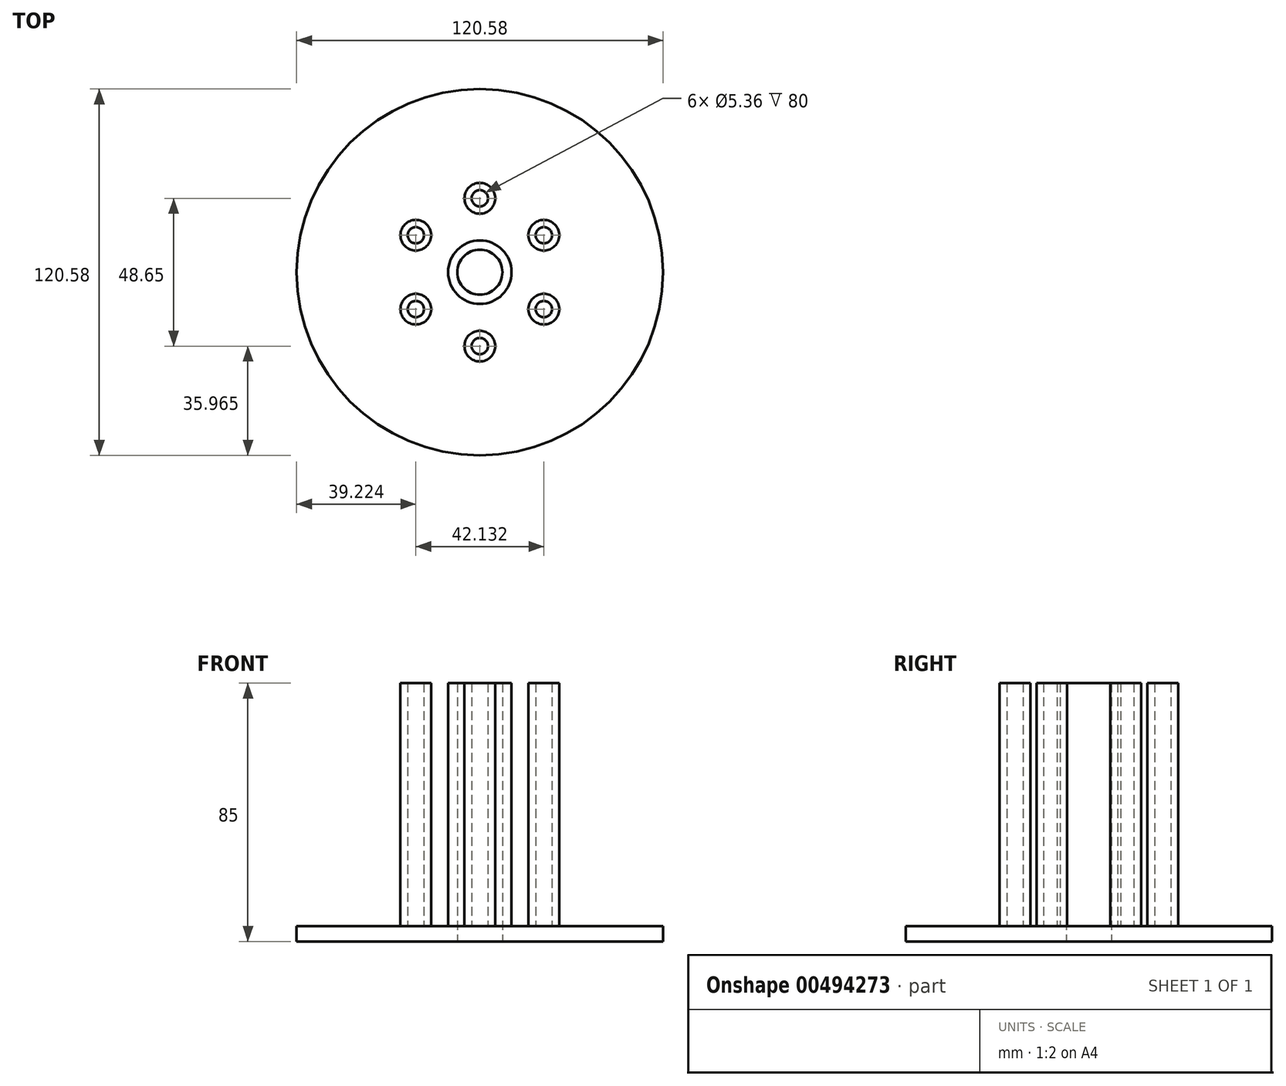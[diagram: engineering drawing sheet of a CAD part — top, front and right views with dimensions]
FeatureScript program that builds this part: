
annotation { "Feature Type Name" : "Feature", "Feature Type Description" : "" }
export const myFeature = defineFeature(function(context is Context, id is Id, definition is map)
    precondition{}
    {
        {
            var Q0;
            Q0=qCreatedBy(makeId("Top.planeOp"),FACE);
            var sketch = newSketch(context, id + "F0", { "sketchPlane" : qUnion([Q0])});
            skCircle(sketch, "E0", {"center": v(0, 0) * mm, "radius": 60.29 * mm});
            skCircle(sketch, "E1", {"center": v(0, 0) * mm, "radius": 7.42 * mm});
            skSolve(sketch);
        }
        {
            var Q0;
            Q0=makeQuery(id+"F0.imprint","IMPRINT",FACE,{"disambiguationData":[TD([[makeQuery(id+"F0.imprint","IMPRINT",EDGE,{"derivedFrom":sQuery(id+"F0.wireOp",EDGE,"E0")}),1.0]])]});
            extrude(context, id + "F1", {"entities" : qUnion([Q0]), "depth" : 5 * mm});
        }
        {
            var Q0;
            Q0=makeQuery(id+"F1.opExtrude","CAP_FACE",FACE,{"disambiguationData":[OSD([sQuery(id+"F0.wireOp",EDGE,"E0"),sQuery(id+"F0.wireOp",EDGE,"E1")])],"isStart":false});
            var sketch = newSketch(context, id + "F2", { "sketchPlane" : qUnion([Q0])});
            skCircle(sketch, "E2", {"center": v(0, 0) * mm, "radius": 10.45 * mm});
            skCircle(sketch, "E3", {"center": v(0, -24.32) * mm, "radius": 2.68 * mm});
            skCircle(sketch, "E4", {"center": v(0, -24.32) * mm, "radius": 5.06 * mm});
            skCircle(sketch, "E5.1.0", {"center": v(21.07, -12.16) * mm, "radius": 5.06 * mm});
            skCircle(sketch, "E5.1.1", {"center": v(21.07, -12.16) * mm, "radius": 2.68 * mm});
            skCircle(sketch, "E5.2.0", {"center": v(21.07, 12.16) * mm, "radius": 5.06 * mm});
            skCircle(sketch, "E5.2.1", {"center": v(21.07, 12.16) * mm, "radius": 2.68 * mm});
            skCircle(sketch, "E5.3.0", {"center": v(0, 24.32) * mm, "radius": 5.06 * mm});
            skCircle(sketch, "E5.3.1", {"center": v(0, 24.32) * mm, "radius": 2.68 * mm});
            skCircle(sketch, "E5.4.0", {"center": v(-21.07, 12.16) * mm, "radius": 5.06 * mm});
            skCircle(sketch, "E5.4.1", {"center": v(-21.07, 12.16) * mm, "radius": 2.68 * mm});
            skCircle(sketch, "E5.5.0", {"center": v(-21.07, -12.16) * mm, "radius": 5.06 * mm});
            skCircle(sketch, "E5.5.1", {"center": v(-21.07, -12.16) * mm, "radius": 2.68 * mm});
            skSolve(sketch);
        }
        {
            var Q0;
            Q0=makeQuery(id+"F2.imprint","IMPRINT",FACE,{"disambiguationData":[TD([[makeQuery(id+"F2.imprint","IMPRINT",EDGE,{"derivedFrom":sQuery(id+"F2.wireOp",EDGE,"E2")}),1.0]])]});
            var Q1;
            Q1=makeQuery(id+"F2.imprint","IMPRINT",FACE,{"disambiguationData":[TD([[makeQuery(id+"F2.imprint","IMPRINT",EDGE,{"derivedFrom":sQuery(id+"F2.wireOp",EDGE,"E3")}),-1.0]])]});
            var Q2;
            Q2=makeQuery(id+"F2.imprint","IMPRINT",FACE,{"disambiguationData":[TD([[makeQuery(id+"F2.imprint","IMPRINT",EDGE,{"derivedFrom":sQuery(id+"F2.wireOp",EDGE,"E5.5.0")}),1.0]])]});
            var Q3;
            Q3=makeQuery(id+"F2.imprint","IMPRINT",FACE,{"disambiguationData":[TD([[makeQuery(id+"F2.imprint","IMPRINT",EDGE,{"derivedFrom":sQuery(id+"F2.wireOp",EDGE,"E5.3.0")}),1.0]])]});
            var Q4;
            Q4=makeQuery(id+"F2.imprint","IMPRINT",FACE,{"disambiguationData":[TD([[makeQuery(id+"F2.imprint","IMPRINT",EDGE,{"derivedFrom":sQuery(id+"F2.wireOp",EDGE,"E5.4.0")}),1.0]])]});
            var Q5;
            Q5=makeQuery(id+"F2.imprint","IMPRINT",FACE,{"disambiguationData":[TD([[makeQuery(id+"F2.imprint","IMPRINT",EDGE,{"derivedFrom":sQuery(id+"F2.wireOp",EDGE,"E5.2.0")}),1.0]])]});
            var Q6;
            Q6=makeQuery(id+"F2.imprint","IMPRINT",FACE,{"disambiguationData":[TD([[makeQuery(id+"F2.imprint","IMPRINT",EDGE,{"derivedFrom":sQuery(id+"F2.wireOp",EDGE,"E5.1.0")}),1.0]])]});
            extrude(context, id + "F3", {"entities" : qUnion([Q0, Q1, Q2, Q3, Q4, Q5, Q6]), "operationType" : NewBodyOperationType.ADD, "depth" : 80 * mm, "offsetDistance" : 25 * mm});
        }
    });
